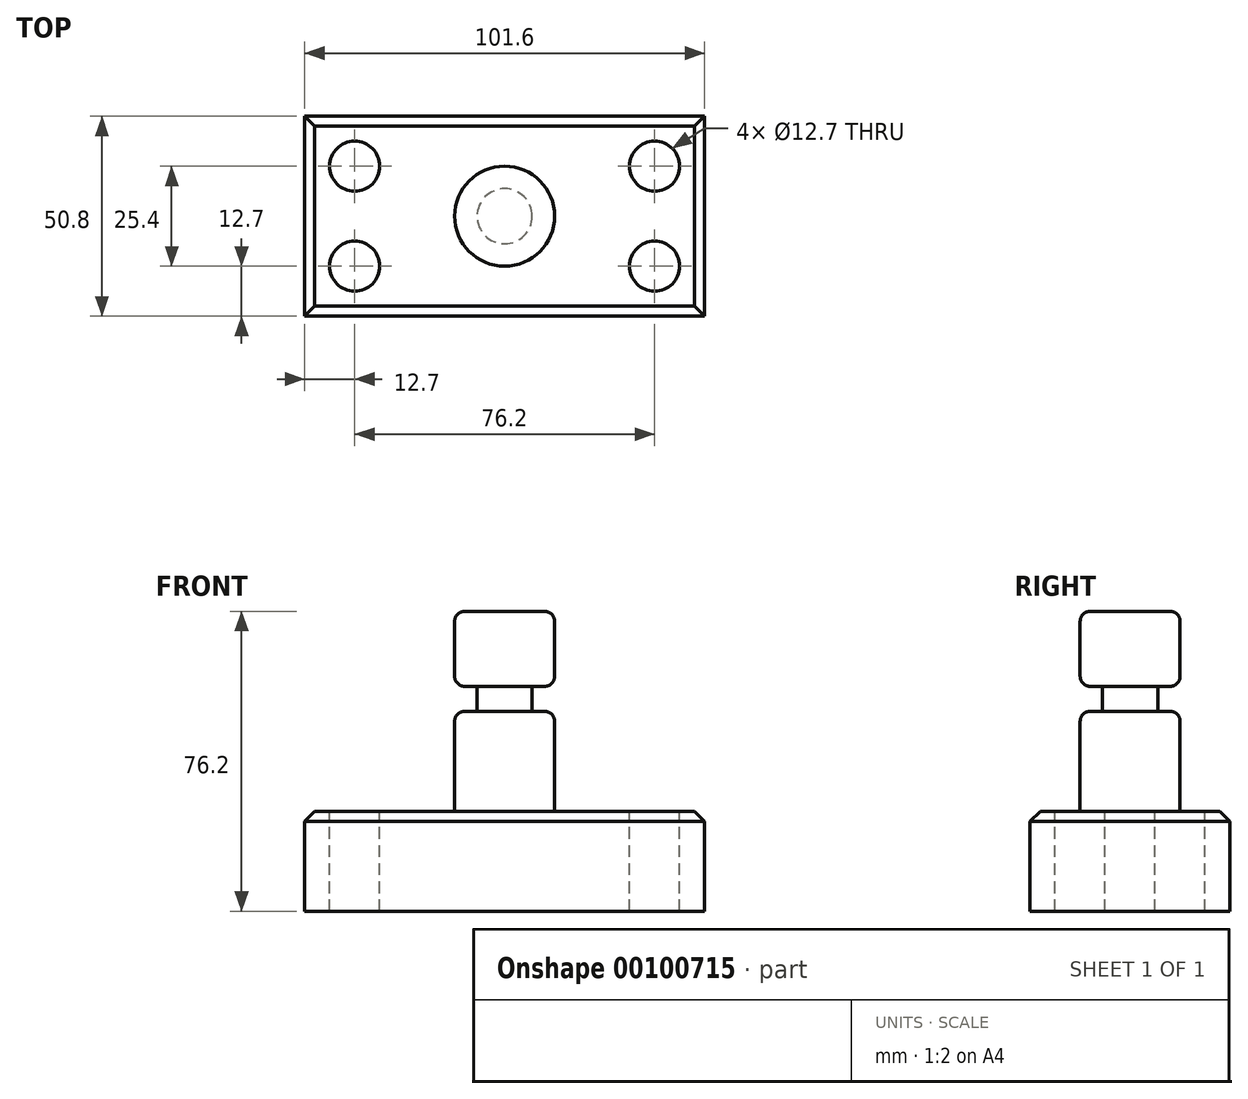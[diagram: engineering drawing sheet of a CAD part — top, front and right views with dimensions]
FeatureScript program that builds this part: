
annotation { "Feature Type Name" : "Feature", "Feature Type Description" : "" }
export const myFeature = defineFeature(function(context is Context, id is Id, definition is map)
    precondition{}
    {
        {
            var Q0;
            Q0=qCreatedBy(makeId("Top.planeOp"),FACE);
            var sketch = newSketch(context, id + "F0", { "sketchPlane" : qUnion([Q0])});
            skLineSegment(sketch, "E0.bottom", {"start": v(50.8, 25.4) * mm, "end": v(-50.8, 25.4) * mm});
            skLineSegment(sketch, "E0.top", {"start": v(50.8, -25.4) * mm, "end": v(-50.8, -25.4) * mm});
            skLineSegment(sketch, "E0.left", {"start": v(-50.8, -25.4) * mm, "end": v(-50.8, 25.4) * mm});
            skLineSegment(sketch, "E0.right", {"start": v(50.8, -25.4) * mm, "end": v(50.8, 25.4) * mm});
            skPoint(sketch, "E0.middle", {"position": v(0, 0) * mm});
            skSolve(sketch);
        }
        {
            var Q0;
            Q0 = qSketchRegion(id + "F0", true);
            extrude(context, id + "F1", {"entities" : qUnion([Q0]), "depth" : 25.4 * mm});
        }
        {
            var Q0;
            Q0=makeQuery(id+"F1.opExtrude","CAP_FACE",FACE,{"disambiguationData":[OSD([sQuery(id+"F0.wireOp",EDGE,"E0.bottom"),sQuery(id+"F0.wireOp",EDGE,"E0.top"),sQuery(id+"F0.wireOp",EDGE,"E0.left"),sQuery(id+"F0.wireOp",EDGE,"E0.right")])],"isStart":false});
            var sketch = newSketch(context, id + "F2", { "sketchPlane" : qUnion([Q0])});
            skCircle(sketch, "E1", {"center": v(38.1, -12.7) * mm, "radius": 6.35 * mm});
            skCircle(sketch, "E2", {"center": v(-38.1, -12.7) * mm, "radius": 6.35 * mm});
            skCircle(sketch, "E3", {"center": v(-38.1, 12.7) * mm, "radius": 6.35 * mm});
            skCircle(sketch, "E4", {"center": v(38.1, 12.7) * mm, "radius": 6.35 * mm});
            skSolve(sketch);
        }
        {
            var Q0;
            Q0 = qSketchRegion(id + "F2", true);
            extrude(context, id + "F3", {"entities" : qUnion([Q0]), "operationType" : NewBodyOperationType.REMOVE, "endBound" : BoundingType.THROUGH_ALL, "oppositeDirection" : true, "depth" : 25.4 * mm});
        }
        {
            var Q0;
            Q0=qCreatedBy(makeId("Front.planeOp"),FACE);
            var sketch = newSketch(context, id + "F4", { "sketchPlane" : qUnion([Q0])});
            skLineSegment(sketch, "E5.bottom", {"start": v(-12.7, 76.2) * mm, "end": v(0, 76.2) * mm});
            skLineSegment(sketch, "E5.top", {"start": v(-12.7, 25.4) * mm, "end": v(0, 25.4) * mm});
            skLineSegment(sketch, "E5.left", {"start": v(-12.7, 76.2) * mm, "end": v(-12.7, 25.4) * mm});
            skLineSegment(sketch, "E5.right", {"start": v(0, 76.2) * mm, "end": v(0, 25.4) * mm});
            skSolve(sketch);
        }
        {
            var Q0;
            Q0 = qSketchRegion(id + "F4", true);
            var Q1;
            Q1=sQuery(id+"F4.wireOp",EDGE,"E5.right");
            revolve(context, id + "F5", {"operationType" : NewBodyOperationType.ADD, "entities" : qUnion([Q0]), "axis" : qUnion([Q1]), "revolveType" : RevolveType.FULL});
        }
        {
            var Q0;
            Q0=qCreatedBy(makeId("Front.planeOp"),FACE);
            var sketch = newSketch(context, id + "F6", { "sketchPlane" : qUnion([Q0])});
            skLineSegment(sketch, "E6.bottom", {"start": v(-23.14, 57.15) * mm, "end": v(-7, 57.15) * mm});
            skLineSegment(sketch, "E6.top", {"start": v(-23.14, 50.8) * mm, "end": v(-7, 50.8) * mm});
            skLineSegment(sketch, "E6.left", {"start": v(-23.14, 57.15) * mm, "end": v(-23.14, 50.8) * mm});
            skLineSegment(sketch, "E6.right", {"start": v(-7, 57.15) * mm, "end": v(-7, 50.8) * mm});
            skLineSegment(sketch, "E7", {"start": v(0, 0) * mm, "end": v(0, 83.59) * mm, "construction": true});
            skSolve(sketch);
        }
        {
            var Q0;
            Q0 = qSketchRegion(id + "F6", true);
            var Q1;
            Q1=sQuery(id+"F6.wireOp",EDGE,"E7");
            revolve(context, id + "F7", {"operationType" : NewBodyOperationType.REMOVE, "entities" : qUnion([Q0]), "axis" : qUnion([Q1]), "revolveType" : RevolveType.FULL, "oppositeDirection" : true});
        }
        {
            var Q0;
            Q0=makeQuery(id+"F5.opRevolve","SWEPT_EDGE",EDGE,{"disambiguationData":[OSD([sQuery(id+"F4.wireOp",EDGE,"E5.bottom"),sQuery(id+"F4.wireOp",EDGE,"E5.left")])]});
            var Q1;
            Q1=makeQuery(id+"F7.boolean.opBoolean","INTERSECT",EDGE,{"derivedFrom":[makeQuery(id+"F5.opRevolve","SWEPT_FACE",FACE,{"disambiguationData":[OSD([sQuery(id+"F4.wireOp",EDGE,"E5.left")])]}),makeQuery(id+"F7.opRevolve","SWEPT_FACE",FACE,{"disambiguationData":[OSD([sQuery(id+"F6.wireOp",EDGE,"E6.bottom")])]})]});
            var Q2;
            Q2=makeQuery(id+"F7.boolean.opBoolean","INTERSECT",EDGE,{"derivedFrom":[makeQuery(id+"F5.opRevolve","SWEPT_FACE",FACE,{"disambiguationData":[OSD([sQuery(id+"F4.wireOp",EDGE,"E5.left")])]}),makeQuery(id+"F7.opRevolve","SWEPT_FACE",FACE,{"disambiguationData":[OSD([sQuery(id+"F6.wireOp",EDGE,"E6.top")])]})]});
            var Q3;
            Q3=makeQuery(id+"F5.opRevolve","SWEPT_EDGE",EDGE,{"disambiguationData":[OSD([sQuery(id+"F4.wireOp",EDGE,"E5.top"),sQuery(id+"F4.wireOp",EDGE,"E5.left")])]});
            var Q4;
            Q4=makeQuery(id+"F3.boolean.opBoolean","COPY",EDGE,{"derivedFrom":makeQuery(id+"F3.opExtrude","CAP_EDGE",EDGE,{"disambiguationData":[OSD([sQuery(id+"F2.wireOp",EDGE,"E2")])],"isStart":true})});
            var Q5;
            Q5=makeQuery(id+"F3.boolean.opBoolean","COPY",EDGE,{"derivedFrom":makeQuery(id+"F3.opExtrude","CAP_EDGE",EDGE,{"disambiguationData":[OSD([sQuery(id+"F2.wireOp",EDGE,"E3")])],"isStart":true})});
            var Q6;
            Q6=makeQuery(id+"F3.boolean.opBoolean","COPY",EDGE,{"derivedFrom":makeQuery(id+"F3.opExtrude","CAP_EDGE",EDGE,{"disambiguationData":[OSD([sQuery(id+"F2.wireOp",EDGE,"E1")])],"isStart":true})});
            var Q7;
            Q7=makeQuery(id+"F3.boolean.opBoolean","COPY",EDGE,{"derivedFrom":makeQuery(id+"F3.opExtrude","CAP_EDGE",EDGE,{"disambiguationData":[OSD([sQuery(id+"F2.wireOp",EDGE,"E4")])],"isStart":true})});
            fillet(context, id + "F8", {"entities" : qUnion([Q0, Q1, Q2, Q3, Q4, Q5, Q6, Q7]), "radius" : 2.54 * mm, "tangentPropagation" : true, "allowEdgeOverflow" : false});
        }
        {
            var Q0;
            Q0=makeQuery(id+"F1.opExtrude","CAP_EDGE",EDGE,{"disambiguationData":[OSD([sQuery(id+"F0.wireOp",EDGE,"E0.left")])],"isStart":false});
            var Q1;
            Q1=makeQuery(id+"F1.opExtrude","CAP_EDGE",EDGE,{"disambiguationData":[OSD([sQuery(id+"F0.wireOp",EDGE,"E0.top")])],"isStart":false});
            var Q2;
            Q2=makeQuery(id+"F1.opExtrude","CAP_EDGE",EDGE,{"disambiguationData":[OSD([sQuery(id+"F0.wireOp",EDGE,"E0.right")])],"isStart":false});
            var Q3;
            Q3=makeQuery(id+"F1.opExtrude","CAP_EDGE",EDGE,{"disambiguationData":[OSD([sQuery(id+"F0.wireOp",EDGE,"E0.bottom")])],"isStart":false});
            chamfer(context, id + "F9", {"entities" : qUnion([Q0, Q1, Q2, Q3]), "width" : 2.54 * mm, "tangentPropagation" : true});
        }
    });
